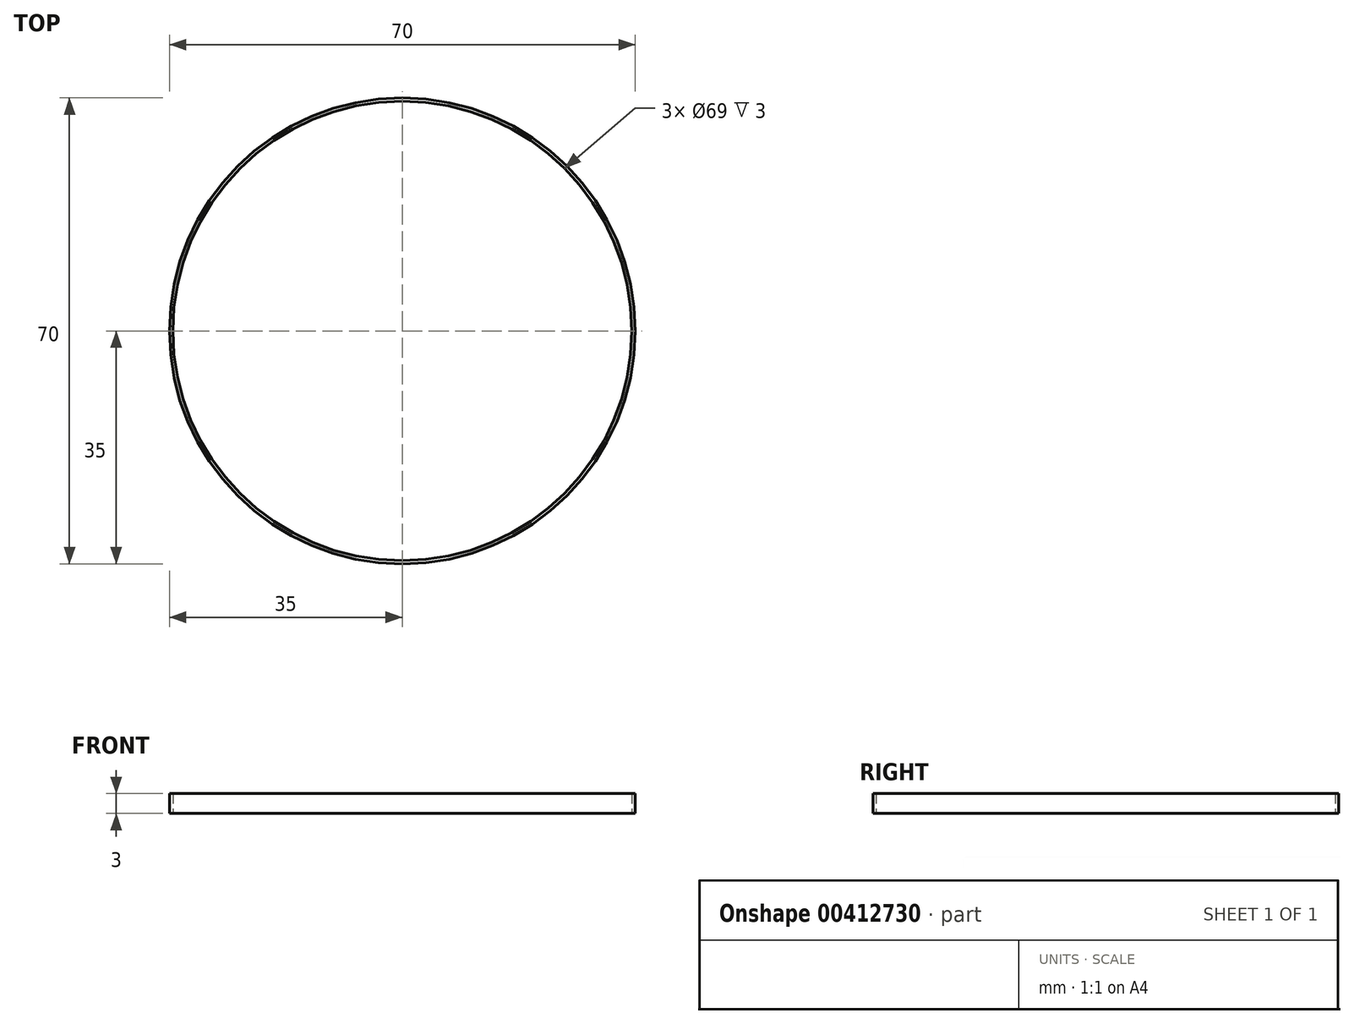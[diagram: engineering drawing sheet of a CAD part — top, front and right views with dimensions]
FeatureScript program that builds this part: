
annotation { "Feature Type Name" : "Feature", "Feature Type Description" : "" }
export const myFeature = defineFeature(function(context is Context, id is Id, definition is map)
    precondition{}
    {
        {
            var Q0;
            Q0=qCreatedBy(makeId("Top.planeOp"),FACE);
            var sketch = newSketch(context, id + "F0", { "sketchPlane" : qUnion([Q0])});
            skCircle(sketch, "E0", {"center": v(0, 0) * mm, "radius": 34.5 * mm});
            skCircle(sketch, "E1", {"center": v(0, 0) * mm, "radius": 35 * mm});
            skSolve(sketch);
        }
        {
            var Q0;
            Q0=makeQuery(id+"F0.imprint","IMPRINT",FACE,{"disambiguationData":[TD([[makeQuery(id+"F0.imprint","IMPRINT",EDGE,{"derivedFrom":sQuery(id+"F0.wireOp",EDGE,"E0")}),-1.0]])]});
            extrude(context, id + "F1", {"entities" : qUnion([Q0]), "depth" : 3 * mm, "offsetDistance" : 25 * mm});
        }
    });
